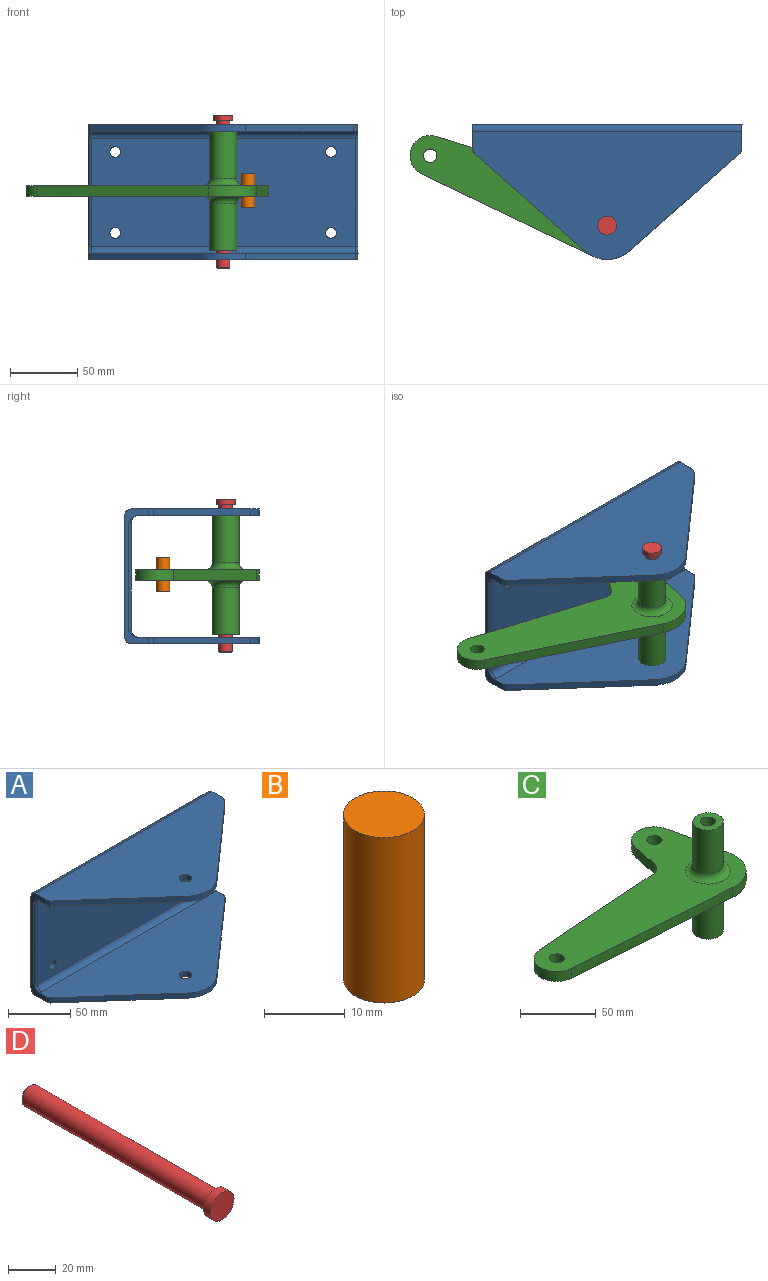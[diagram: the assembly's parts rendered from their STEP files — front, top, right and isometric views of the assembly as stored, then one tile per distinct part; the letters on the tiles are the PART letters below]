
ASSEMBLY  parts=4 mates=3
PART A: 34 faces, bbox 218.8x100x100 mm
  f0: plane 200x90mm, normal (0,1,0), area 17798.9mm2, adj f1,f6,f16,f17,f18,f19,f32,f33
  f1: plane 100x17.75mm, normal (-1,0,0), area 457.6mm2, adj f0,f7,f8,f14,f15,f21,f23,f25
  f2: plane 81.76x72.24mm, normal (-0.66,-0.75,0), area 545.5mm2, adj f3,f7,f8,f21
  f3: cylinder r=25mm len=33.11mm, axis (0,0,-1), area 180.9mm2, adj f2,f4,f7,f8
  f4: plane 80.07x70.75mm, normal (0.66,-0.75,0), area 534.2mm2, adj f3,f7,f8,f20
  f5: cylinder r=5mm len=10mm, axis (0,0,-1), area 157.1mm2, adj f7,f8
  f6: plane 100x17.75mm, normal (1,0,0), area 446.3mm2, adj f0,f7,f8,f14,f15,f20,f22,f24
  f7: plane 200x95mm, normal (0,0,1), area 11654.2mm2, adj f1,f2,f3,f4,f5,f6,f20,f21
  f8: plane 200x90.29mm, normal (0,0,-1), area 10654.6mm2, adj f1,f2,f3,f4,f5,f6,f20,f21
  f9: plane 196x80mm, normal (0,-1,0), area 15478.9mm2, adj f16,f17,f18,f19,f24,f25,f27,f30
  f10: plane 81.76x72.24mm, normal (-0.66,-0.75,0), area 545.5mm2, adj f11,f14,f15,f23
  f11: cylinder r=25mm len=33.11mm, axis (0,0,-1), area 180.9mm2, adj f10,f12,f14,f15
  f12: plane 81.76x72.24mm, normal (0.66,-0.75,0), area 545.5mm2, adj f11,f14,f15,f22
  f13: cylinder r=5mm len=10mm, axis (0,0,-1), area 157.1mm2, adj f14,f15
  f14: plane 200x90.29mm, normal (0,0,1), area 10656.7mm2, adj f1,f6,f10,f11,f12,f13,f22,f23
  f15: plane 200x95mm, normal (0,0,-1), area 11656.3mm2, adj f1,f6,f10,f11,f12,f13,f22,f23
  f16: cylinder r=4mm len=8mm, axis (0,1,0), area 125.7mm2, adj f0,f9
  f17: cylinder r=4mm len=8mm, axis (0,1,0), area 125.7mm2, adj f0,f9
  f18: cylinder r=4mm len=8mm, axis (0,1,0), area 125.7mm2, adj f0,f9
  f19: cylinder r=4mm len=8mm, axis (0,1,0), area 125.7mm2, adj f0,f9
  f20: cylinder r=10mm len=7.49mm, axis (0,0,1), area 42.4mm2, adj f4,f6,f7,f8
  f21: cylinder r=5mm len=5mm, axis (0,0,1), area 21.2mm2, adj f1,f2,f7,f8
  f22: cylinder r=5mm len=5mm, axis (0,0,1), area 21.2mm2, adj f6,f12,f14,f15
  f23: cylinder r=5mm len=5mm, axis (0,0,1), area 21.2mm2, adj f1,f10,f14,f15
  f24: cylinder r=2mm len=80mm, axis (0,0,1), area 251.3mm2, adj f6,f9,f26,f29
  f25: cylinder r=2mm len=80mm, axis (0,0,-1), area 251.3mm2, adj f1,f9,f28,f31
  f26: torus R=7mm, axis (0,0,1), area 17.8mm2, adj f6,f14,f24,f27
  f27: cylinder r=5mm len=196mm, axis (-1,0,0), area 1539.4mm2, adj f9,f14,f26,f28
  f28: torus R=7mm, axis (0,0,1), area 17.8mm2, adj f1,f14,f25,f27
  f29: torus R=7mm, axis (0,0,1), area 17.8mm2, adj f6,f8,f24,f30
  f30: cylinder r=5mm len=196mm, axis (1,0,0), area 1539.4mm2, adj f8,f9,f29,f31
  f31: torus R=7mm, axis (0,0,1), area 17.8mm2, adj f1,f8,f25,f30
  f32: cylinder r=5mm len=200mm, axis (-1,0,0), area 1570.8mm2, adj f0,f1,f6,f15
  f33: cylinder r=5mm len=200mm, axis (1,0,0), area 1570.8mm2, adj f0,f1,f6,f7
PART B: 3 faces, bbox 10x10x25 mm
  f0: cylinder r=5mm len=25mm, axis (0,0,-1), area 785.4mm2, adj f1,f2
  f1: plane 10x10mm, normal (0,0,1), area 78.5mm2, adj f0
  f2: plane 10x10mm, normal (0,0,-1), area 78.5mm2, adj f0
PART C: 19 faces, bbox 181.1x90x88 mm
  f0: plane 140.39x9.98mm, normal (-0.07,-1,0), area 1126mm2, adj f1,f7,f10,f11
  f1: cylinder r=25mm len=30mm, axis (0,0,-1), area 368.6mm2, adj f0,f2,f10,f11
  f2: plane 48x9.8mm, normal (0.98,0.2,0), area 391.9mm2, adj f1,f3,f10,f11
  f3: cylinder r=15mm len=29.39mm, axis (0,0,-1), area 328.7mm2, adj f2,f4,f10,f11
  f4: plane 21.97x8mm, normal (-0.98,0.2,0), area 179.4mm2, adj f3,f5,f10,f11
  f5: cylinder r=10mm len=9.09mm, axis (0,0,-1), area 103.9mm2, adj f4,f6,f10,f11
  f6: plane 113.89x8.09mm, normal (-0.07,1,0), area 913.4mm2, adj f5,f7,f10,f11
  f7: cylinder r=15mm len=29.92mm, axis (0,0,-1), area 360mm2, adj f0,f6,f10,f11
  f8: cylinder r=5mm len=10mm, axis (0,0,-1), area 251.3mm2, adj f10,f11
  f9: cylinder r=5mm len=10mm, axis (0,0,-1), area 251.3mm2, adj f10,f11
  f10: plane 181.1x90mm, normal (0,0,1), area 7483.6mm2, adj f0,f1,f2,f3,f4,f5,f6,f7
  f11: plane 181.1x90mm, normal (0,0,-1), area 7483.6mm2, adj f0,f1,f2,f3,f4,f5,f6,f7
  f12: plane 20x20mm, normal (0,0,-1), area 235.6mm2, adj f13,f14
  f13: cylinder r=10mm len=35mm, axis (0,0,-1), area 2199.1mm2, adj f12,f18
  f14: cylinder r=5mm len=88mm, axis (0,0,-1), area 2764.6mm2, adj f12,f16
  f15: cylinder r=10mm len=35mm, axis (0,0,-1), area 2199.1mm2, adj f16,f17
  f16: plane 20x20mm, normal (0,0,1), area 235.6mm2, adj f14,f15
  f17: torus R=15mm, axis (0,0,1), area 583.1mm2, adj f10,f15
  f18: torus R=15mm, axis (0,0,1), area 583.1mm2, adj f11,f13
PART D: 6 faces, bbox 14x114x14 mm
  f0: cylinder r=5mm len=109mm, axis (0,-1,0), area 3424.3mm2, adj f2,f5
  f1: plane 8x8mm, normal (0,1,0), area 50.3mm2, adj f2
  f2: cone r=5mm half-angle=45deg, axis (0,-1,0), area 40mm2, adj f0,f1
  f3: cylinder r=7mm len=14mm, axis (0,1,0), area 175.9mm2, adj f4,f5
  f4: plane 14x14mm, normal (0,-1,0), area 153.9mm2, adj f3
  f5: plane 14x14mm, normal (0,1,0), area 75.4mm2, adj f0,f3
PLACE A rot(axis=(0.03,-0.05,-1),0deg) t=(-89.27,83.65,78.41)mm
PLACE B rot(axis=(0,0,-1),21.6deg) t=(-89.27,8.65,67.36)mm
PLACE C rot(axis=(0,0,-1),21.6deg) t=(-89.27,8.65,79.41)mm
PLACE D rot(axis=(-1,0,0),90deg) t=(-89.27,8.65,131.7)mm
MATE revolute C.f14 <-> A.f5  axis (0,0,1) through (-89.27,8.65,123.41)mm
MATE slider D.f0 <-> A.f5  axis (0,0,1) through (-89.27,8.65,77.2)mm
MATE slider B.f0 <-> C.f8  axis (0,0,-1) through (-70.88,55.14,79.86)mm
